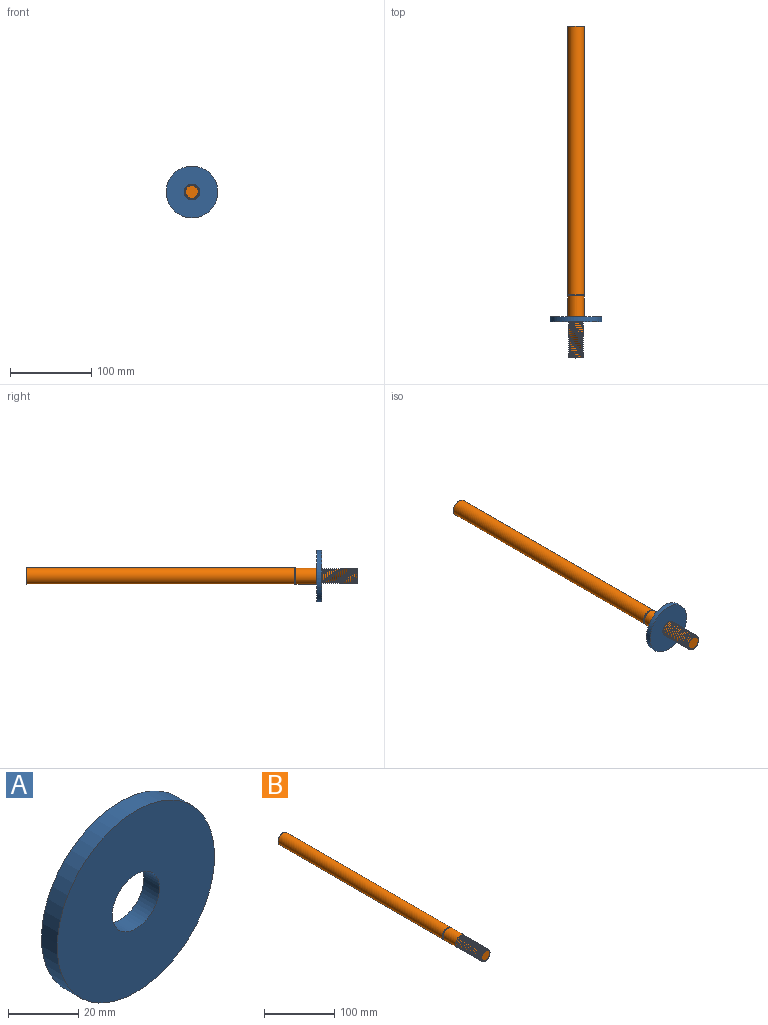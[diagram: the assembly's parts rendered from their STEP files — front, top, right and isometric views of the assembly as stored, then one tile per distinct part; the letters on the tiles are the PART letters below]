
ASSEMBLY  parts=2 mates=1
PART A: 4 faces, bbox 63.5x6.4x63.5 mm
  f0: cylinder r=9.53mm len=19.05mm, axis (0,1,0), area 380mm2, adj f2,f3
  f1: cylinder r=31.75mm len=63.5mm, axis (0,1,0), area 1266.8mm2, adj f2,f3
  f2: plane 63.5x63.5mm, normal (0,-1,0), area 2881.9mm2, adj f0,f1
  f3: plane 63.5x63.5mm, normal (0,1,0), area 2881.9mm2, adj f0,f1
PART B: 12 faces, bbox 21.3x410.4x23.3 mm
  f0: cylinder r=9.53mm len=50.8mm, axis (0,1,0), area -381.3mm2, adj f2,f4,f5,f6,f7
  f1: cylinder r=10mm len=25.4mm, axis (0,1,0), area 1595.9mm2, adj f2,f3
  f2: plane 20x20mm, normal (0,-1,0), area 29.1mm2, adj f0,f1
  f3: plane 20x20mm, normal (0,1,0), area 30.6mm2, adj f1,f8
  f4: plane 18.9x18.87mm, normal (0,-1,0), area 243.1mm2, adj f0,f6,f7
  f5: plane 2.29x1.65mm, normal (0,0,-1), area 1.9mm2, adj f0,f6,f7
  f6: bspline ~51.94x22mm, area 2159.7mm2, adj f0,f4,f5,f7
  f7: bspline ~51.1x22mm, area 2127.4mm2, adj f0,f4,f5,f6
  f8: cylinder r=9.5mm len=19mm, axis (0,-1,0), area 75.8mm2, adj f3,f11
  f9: cylinder r=10mm len=330.2mm, axis (0,-1,0), area 20747.1mm2, adj f10,f11
  f10: plane 20x20mm, normal (0,1,0), area 314.2mm2, adj f9
  f11: plane 20x20mm, normal (0,-1,0), area 30.6mm2, adj f8,f9
PLACE A t=(30.96,-75.62,88.23)mm
PLACE B t=(30.96,-50.22,88.23)mm
MATE fastened A.f0 <-> B.f1  axis (0,1,0) through (30.96,-75.62,88.23)mm
